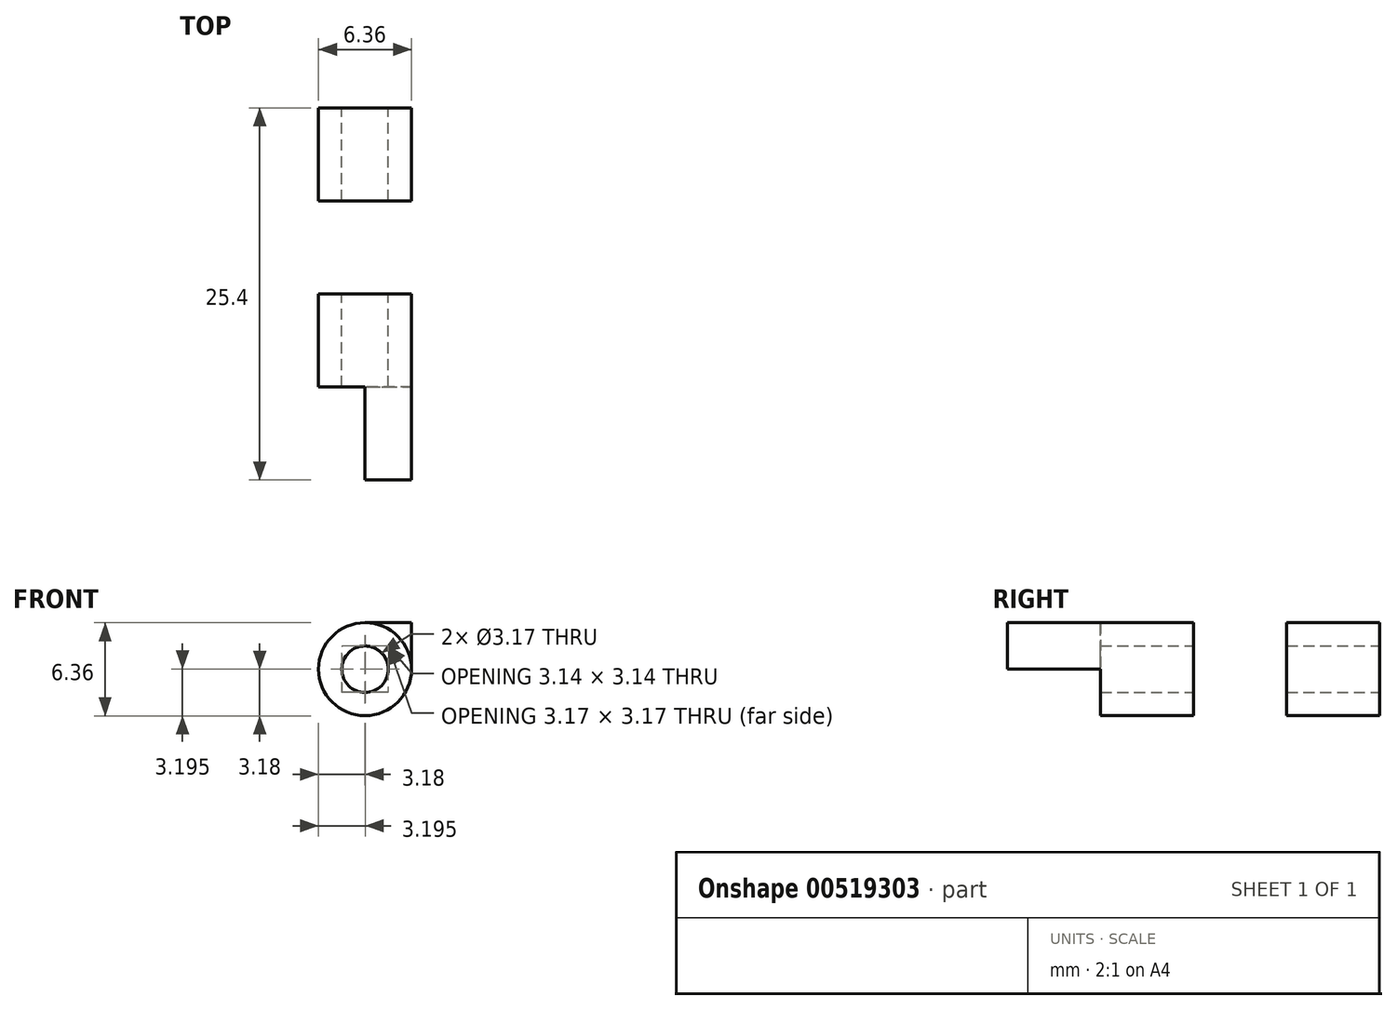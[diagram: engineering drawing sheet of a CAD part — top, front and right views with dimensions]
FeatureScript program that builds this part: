
annotation { "Feature Type Name" : "Feature", "Feature Type Description" : "" }
export const myFeature = defineFeature(function(context is Context, id is Id, definition is map)
    precondition{}
    {
        {
            var Q0;
            Q0=qCreatedBy(makeId("Front.planeOp"),FACE);
            var sketch = newSketch(context, id + "F0", { "sketchPlane" : qUnion([Q0])});
            skLineSegment(sketch, "E0.top", {"start": v(0, 12.7) * mm, "end": v(3.17, 12.7) * mm});
            skLineSegment(sketch, "E0.left", {"start": v(0, 3.18) * mm, "end": v(0, 12.7) * mm});
            skLineSegment(sketch, "E0.right", {"start": v(3.18, 0) * mm, "end": v(3.17, 12.7) * mm});
            skArc(sketch, "E1", {"start": v(0, 3.18) * mm, "mid": v(-2.25, -2.25) * mm, "end": v(3.18, 0) * mm});
            skCircle(sketch, "E2", {"center": v(0, 0) * mm, "radius": 1.59 * mm});
            skSolve(sketch);
        }
        {
            var Q0;
            Q0=makeQuery(id+"F0.imprint","IMPRINT",FACE,{"disambiguationData":[TD([[makeQuery(id+"F0.imprint","IMPRINT",EDGE,{"derivedFrom":sQuery(id+"F0.wireOp",EDGE,"E0.top")}),-1.0]])]});
            extrude(context, id + "F1", {"entities" : qUnion([Q0]), "depth" : 25.4 * mm, "offsetDistance" : 25.4 * mm});
        }
        {
            var Q0;
            Q0=makeQuery(id+"F1.opExtrude","CAP_FACE",FACE,{"disambiguationData":[OSD([sQuery(id+"F0.wireOp",EDGE,"E0.top"),sQuery(id+"F0.wireOp",EDGE,"E0.left"),sQuery(id+"F0.wireOp",EDGE,"E0.right"),sQuery(id+"F0.wireOp",EDGE,"E1"),sQuery(id+"F0.wireOp",EDGE,"E2")])],"isStart":false});
            cPlane(context, id + "F2", {"entities" : qUnion([Q0]), "cplaneType" : CPlaneType.OFFSET, "offset" : 12.7 * mm, "oppositeDirection" : true, "width" : 152.4 * mm, "height" : 152.4 * mm});
        }
        {
            var Q0;
            Q0=makeQuery(id+"F1.opExtrude","CAP_FACE",FACE,{"disambiguationData":[OSD([sQuery(id+"F0.wireOp",EDGE,"E0.top"),sQuery(id+"F0.wireOp",EDGE,"E0.left"),sQuery(id+"F0.wireOp",EDGE,"E0.right"),sQuery(id+"F0.wireOp",EDGE,"E1"),sQuery(id+"F0.wireOp",EDGE,"E2")])],"isStart":false});
            var sketch = newSketch(context, id + "F3", { "sketchPlane" : qUnion([Q0])});
            skCircle(sketch, "E3", {"center": v(0, 0) * mm, "radius": 3.18 * mm});
            skSolve(sketch);
        }
        {
            var Q0;
            Q0=qCreatedBy(id+"F2.planeOp",FACE);
            var sketch = newSketch(context, id + "F4", { "sketchPlane" : qUnion([Q0])});
            skCircle(sketch, "E4", {"center": v(0, 0) * mm, "radius": 3.18 * mm, "construction": true});
            skCircle(sketch, "E5", {"center": v(0, 0) * mm, "radius": 3.17 * mm});
            skSolve(sketch);
        }
        {
            var Q0;
            Q0 = qSketchRegion(id + "F4", true);
            var Q1;
            Q1 = qSketchRegion(id + "F3", true);
            extrude(context, id + "F5", {"entities" : qUnion([Q0, Q1]), "operationType" : NewBodyOperationType.REMOVE, "oppositeDirection" : true, "depth" : 6.35 * mm, "offsetDistance" : 25.4 * mm});
        }
        {
            var Q0;
            Q0=makeQuery(id+"F1.opExtrude","SWEPT_FACE",FACE,{"disambiguationData":[OSD([sQuery(id+"F0.wireOp",EDGE,"E0.right")])]});
            var sketch = newSketch(context, id + "F6", { "sketchPlane" : qUnion([Q0])});
            skLineSegment(sketch, "E6", {"start": v(-25.4, 6.35) * mm, "end": v(0, 6.35) * mm, "construction": true});
            skPoint(sketch, "E7", {"position": v(-19.05, 6.35) * mm});
            skPoint(sketch, "E8", {"position": v(-6.35, 6.35) * mm});
            skSolve(sketch);
        }
        {
            var Q0;
            Q0=sQuery(id+"F6.wireOp",VERTEX,"E7");
            var Q1;
            Q1=sQuery(id+"F6.wireOp",VERTEX,"E8");
            var Q2;
            Q2=makeQuery(id+"F1.opExtrude","SWEPT_BODY",BODY,{"disambiguationData":[OSD([sQuery(id+"F0.wireOp",EDGE,"E0.top"),sQuery(id+"F0.wireOp",EDGE,"E0.left"),sQuery(id+"F0.wireOp",EDGE,"E0.right"),sQuery(id+"F0.wireOp",EDGE,"E1"),sQuery(id+"F0.wireOp",EDGE,"E2")])]});
            hole(context, id + "F7", {"style" : HoleStyle.SIMPLE, "endStyle" : HoleEndStyle.THROUGH, "holeDiameter" : 3.17 * mm, "isTappedThrough" : true, "tappedDepth" : 12.7 * mm, "tapClearance" : 3, "locations" : qUnion([Q0, Q1]), "scope" : qUnion([Q2])});
        }
        {
            var Q0;
            Q0=makeQuery(id+"F1.opExtrude","SWEPT_FACE",FACE,{"disambiguationData":[OSD([sQuery(id+"F0.wireOp",EDGE,"E0.left")])]});
            var sketch = newSketch(context, id + "F8", { "sketchPlane" : qUnion([Q0])});
            skLineSegment(sketch, "E9.bottom", {"start": v(12.7, 3.17) * mm, "end": v(6.35, 3.17) * mm});
            skLineSegment(sketch, "E9.top", {"start": v(12.7, 0) * mm, "end": v(6.35, 0) * mm});
            skLineSegment(sketch, "E9.left", {"start": v(12.7, 3.17) * mm, "end": v(12.7, 0) * mm});
            skLineSegment(sketch, "E9.right", {"start": v(6.35, 3.17) * mm, "end": v(6.35, 0) * mm});
            skLineSegment(sketch, "E10.bottom", {"start": v(19.05, 3.18) * mm, "end": v(25.4, 3.18) * mm});
            skLineSegment(sketch, "E10.top", {"start": v(19.05, 0) * mm, "end": v(25.4, 0) * mm});
            skLineSegment(sketch, "E10.left", {"start": v(19.05, 3.18) * mm, "end": v(19.05, 0) * mm});
            skLineSegment(sketch, "E10.right", {"start": v(25.4, 3.18) * mm, "end": v(25.4, 0) * mm});
            skSolve(sketch);
        }
        {
            var Q0;
            Q0=makeQuery(id+"F8.imprint","IMPRINT",FACE,{"disambiguationData":[TD([[makeQuery(id+"F8.imprint","IMPRINT",EDGE,{"derivedFrom":sQuery(id+"F8.wireOp",EDGE,"E9.bottom")}),-1.0]])]});
            var Q1;
            Q1=makeQuery(id+"F8.imprint","IMPRINT",FACE,{"disambiguationData":[TD([[makeQuery(id+"F8.imprint","IMPRINT",EDGE,{"derivedFrom":sQuery(id+"F8.wireOp",EDGE,"E10.bottom")}),-1.0]])]});
            extrude(context, id + "F9", {"entities" : qUnion([Q0, Q1]), "operationType" : NewBodyOperationType.REMOVE, "endBound" : BoundingType.THROUGH_ALL, "oppositeDirection" : true, "depth" : 25.4 * mm, "offsetDistance" : 25.4 * mm});
        }
    });
